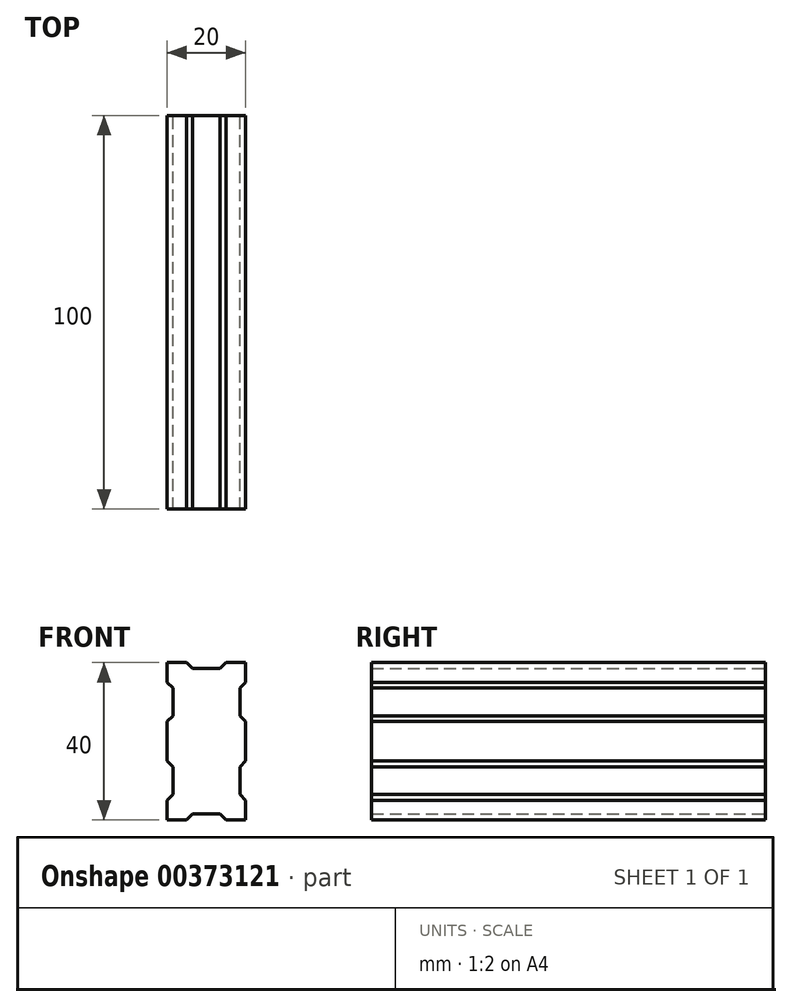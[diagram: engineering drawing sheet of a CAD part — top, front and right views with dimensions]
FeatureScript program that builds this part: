
annotation { "Feature Type Name" : "Feature", "Feature Type Description" : "" }
export const myFeature = defineFeature(function(context is Context, id is Id, definition is map)
    precondition{}
    {
        {
            var Q0;
            Q0=qCreatedBy(makeId("Front.planeOp"),FACE);
            var sketch = newSketch(context, id + "F0", { "sketchPlane" : qUnion([Q0])});
            skLineSegment(sketch, "E0", {"start": v(0, 0) * mm, "end": v(5, 0) * mm});
            skLineSegment(sketch, "E1", {"start": v(5, 0) * mm, "end": v(6.5, 1.5) * mm});
            skLineSegment(sketch, "E2", {"start": v(6.5, 1.5) * mm, "end": v(13.5, 1.5) * mm});
            skLineSegment(sketch, "E3", {"start": v(13.5, 1.5) * mm, "end": v(15, 0) * mm});
            skLineSegment(sketch, "E4", {"start": v(15, 0) * mm, "end": v(20, 0) * mm});
            skLineSegment(sketch, "E5", {"start": v(20, 0) * mm, "end": v(20, 5) * mm});
            skLineSegment(sketch, "E6", {"start": v(20, 5) * mm, "end": v(18.5, 6.5) * mm});
            skLineSegment(sketch, "E7", {"start": v(18.5, 6.5) * mm, "end": v(18.5, 13.5) * mm});
            skLineSegment(sketch, "E8", {"start": v(18.5, 13.5) * mm, "end": v(20, 15) * mm});
            skLineSegment(sketch, "E9", {"start": v(20, 15) * mm, "end": v(20, 25) * mm});
            skLineSegment(sketch, "E10", {"start": v(20, 25) * mm, "end": v(18.5, 26.5) * mm});
            skLineSegment(sketch, "E11", {"start": v(18.5, 26.5) * mm, "end": v(18.5, 33.5) * mm});
            skLineSegment(sketch, "E12", {"start": v(18.5, 33.5) * mm, "end": v(20, 35) * mm});
            skLineSegment(sketch, "E13", {"start": v(20, 35) * mm, "end": v(20, 40) * mm});
            skLineSegment(sketch, "E14", {"start": v(20, 40) * mm, "end": v(15, 40) * mm});
            skLineSegment(sketch, "E15", {"start": v(15, 40) * mm, "end": v(13.5, 38.5) * mm});
            skLineSegment(sketch, "E16", {"start": v(13.5, 38.5) * mm, "end": v(6.5, 38.5) * mm});
            skLineSegment(sketch, "E17", {"start": v(6.5, 38.5) * mm, "end": v(5, 40) * mm});
            skLineSegment(sketch, "E18", {"start": v(5, 40) * mm, "end": v(0, 40) * mm});
            skLineSegment(sketch, "E19", {"start": v(0, 40) * mm, "end": v(0, 35) * mm});
            skLineSegment(sketch, "E20", {"start": v(0, 35) * mm, "end": v(1.5, 33.5) * mm});
            skLineSegment(sketch, "E21", {"start": v(1.5, 33.5) * mm, "end": v(1.5, 26.5) * mm});
            skLineSegment(sketch, "E22", {"start": v(1.5, 26.5) * mm, "end": v(0, 25) * mm});
            skLineSegment(sketch, "E23", {"start": v(0, 25) * mm, "end": v(0, 15) * mm});
            skLineSegment(sketch, "E24", {"start": v(0, 15) * mm, "end": v(1.5, 13.5) * mm});
            skLineSegment(sketch, "E25", {"start": v(1.5, 13.5) * mm, "end": v(1.5, 6.5) * mm});
            skLineSegment(sketch, "E26", {"start": v(1.5, 6.5) * mm, "end": v(0, 5) * mm});
            skLineSegment(sketch, "E27", {"start": v(0, 5) * mm, "end": v(0, 0) * mm});
            skSolve(sketch);
        }
        {
            var Q0;
            Q0 = qSketchRegion(id + "F0", true);
            extrude(context, id + "F1", {"entities" : qUnion([Q0]), "depth" : 100 * mm});
        }
    });
